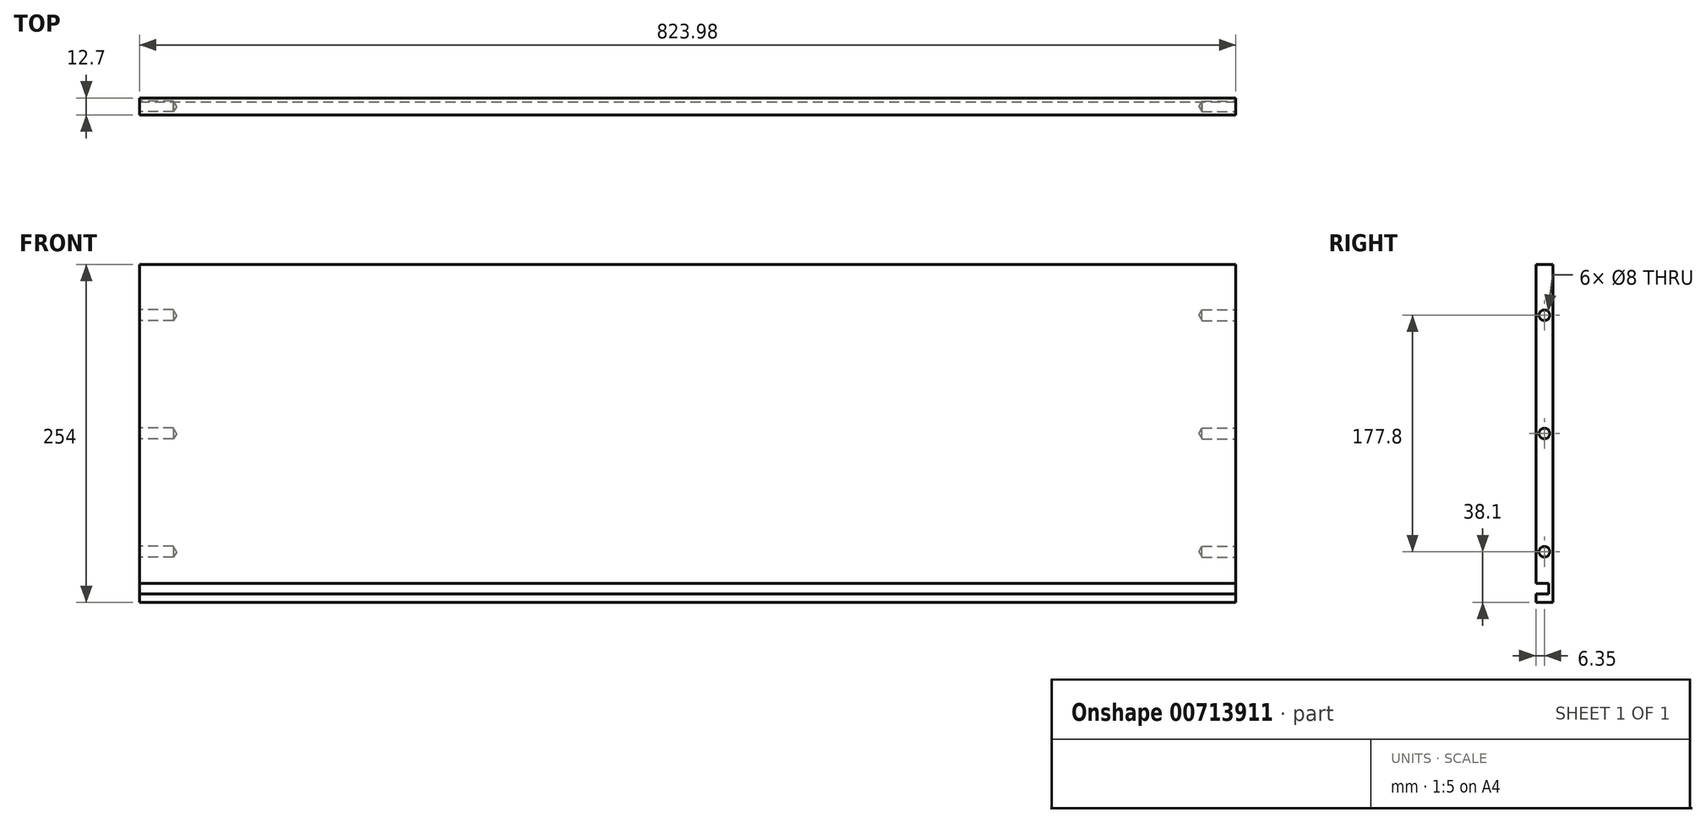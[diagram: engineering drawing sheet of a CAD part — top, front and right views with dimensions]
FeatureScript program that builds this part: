
annotation { "Feature Type Name" : "Feature", "Feature Type Description" : "" }
export const myFeature = defineFeature(function(context is Context, id is Id, definition is map)
    precondition{}
    {
        {
            var Q0;
            Q0=qCreatedBy(makeId("Front.planeOp"),FACE);
            var sketch = newSketch(context, id + "F0", { "sketchPlane" : qUnion([Q0])});
            skLineSegment(sketch, "E0.bottom", {"start": v(411.99, 127) * mm, "end": v(-411.99, 127) * mm});
            skLineSegment(sketch, "E0.top", {"start": v(411.99, -127) * mm, "end": v(-411.99, -127) * mm});
            skLineSegment(sketch, "E0.left", {"start": v(411.99, 127) * mm, "end": v(411.99, -127) * mm});
            skLineSegment(sketch, "E0.right", {"start": v(-411.99, 127) * mm, "end": v(-411.99, -127) * mm});
            skPoint(sketch, "E0.middle", {"position": v(0, 0) * mm});
            skSolve(sketch);
        }
        {
            var Q0;
            Q0=makeQuery(id+"F0.imprint","IMPRINT",FACE,{"disambiguationData":[TD([[makeQuery(id+"F0.imprint","IMPRINT",EDGE,{"derivedFrom":sQuery(id+"F0.wireOp",EDGE,"E0.bottom")}),1.0]])]});
            extrude(context, id + "F1", {"entities" : qUnion([Q0]), "depth" : 12.7 * mm, "offsetDistance" : 25.4 * mm});
        }
        {
            var Q0;
            Q0=makeQuery(id+"F1.opExtrude","CAP_FACE",FACE,{"disambiguationData":[OSD([sQuery(id+"F0.wireOp",EDGE,"E0.bottom"),sQuery(id+"F0.wireOp",EDGE,"E0.top"),sQuery(id+"F0.wireOp",EDGE,"E0.left"),sQuery(id+"F0.wireOp",EDGE,"E0.right")])],"isStart":false});
            var sketch = newSketch(context, id + "F2", { "sketchPlane" : qUnion([Q0])});
            skLineSegment(sketch, "E1", {"start": v(-411.99, -127) * mm, "end": v(-411.99, -120.65) * mm});
            skLineSegment(sketch, "E2.bottom", {"start": v(-411.99, -120.65) * mm, "end": v(411.99, -120.65) * mm});
            skLineSegment(sketch, "E2.top", {"start": v(-411.99, -112.78) * mm, "end": v(411.99, -112.78) * mm});
            skLineSegment(sketch, "E2.left", {"start": v(-411.99, -120.65) * mm, "end": v(-411.99, -112.78) * mm});
            skLineSegment(sketch, "E2.right", {"start": v(411.99, -120.65) * mm, "end": v(411.99, -112.78) * mm});
            skSolve(sketch);
        }
        {
            var Q0;
            Q0=makeQuery(id+"F2.imprint","IMPRINT",FACE,{"disambiguationData":[TD([[makeQuery(id+"F2.imprint","IMPRINT",EDGE,{"derivedFrom":sQuery(id+"F2.wireOp",EDGE,"E2.bottom")}),1.0]])]});
            extrude(context, id + "F3", {"entities" : qUnion([Q0]), "operationType" : NewBodyOperationType.REMOVE, "oppositeDirection" : true, "depth" : 9.65 * mm, "offsetDistance" : 25.4 * mm});
        }
        {
            var Q0;
            Q0=makeQuery(id+"F1.opExtrude","SWEPT_FACE",FACE,{"disambiguationData":[OSD([sQuery(id+"F0.wireOp",EDGE,"E0.right")])]});
            var sketch = newSketch(context, id + "F4", { "sketchPlane" : qUnion([Q0])});
            skLineSegment(sketch, "E3", {"start": v(6.35, 127) * mm, "end": v(6.35, 88.9) * mm});
            skLineSegment(sketch, "E4", {"start": v(6.35, 88.9) * mm, "end": v(6.35, 0) * mm});
            skLineSegment(sketch, "E5", {"start": v(6.35, 0) * mm, "end": v(6.35, -88.9) * mm});
            skPoint(sketch, "E6", {"position": v(6.35, 88.9) * mm});
            skPoint(sketch, "E7", {"position": v(6.35, 0) * mm});
            skPoint(sketch, "E8", {"position": v(6.35, -88.9) * mm});
            skSolve(sketch);
        }
        {
            var Q0;
            Q0=sQuery(id+"F4.wireOp",VERTEX,"E6");
            var Q1;
            Q1=sQuery(id+"F4.wireOp",VERTEX,"E7");
            var Q2;
            Q2=sQuery(id+"F4.wireOp",VERTEX,"E8");
            var Q3;
            Q3=makeQuery(id+"F1.opExtrude","SWEPT_BODY",BODY,{"disambiguationData":[OSD([sQuery(id+"F0.wireOp",EDGE,"E0.bottom"),sQuery(id+"F0.wireOp",EDGE,"E0.top"),sQuery(id+"F0.wireOp",EDGE,"E0.left"),sQuery(id+"F0.wireOp",EDGE,"E0.right")])]});
            hole(context, id + "F5", {"style" : HoleStyle.SIMPLE, "endStyle" : HoleEndStyle.BLIND, "holeDiameter" : 8 * mm, "majorDiameter" : 6.35 * mm, "holeDepth" : 25.4 * mm, "isTappedThrough" : true, "tappedDepth" : 12.7 * mm, "tapClearance" : 3, "startFromSketch" : true, "locations" : qUnion([Q0, Q1, Q2]), "scope" : qUnion([Q3])});
        }
        {
            var Q0;
            Q0=makeQuery(id+"F1.opExtrude","SWEPT_FACE",FACE,{"disambiguationData":[OSD([sQuery(id+"F0.wireOp",EDGE,"E0.left")])]});
            var sketch = newSketch(context, id + "F6", { "sketchPlane" : qUnion([Q0])});
            skLineSegment(sketch, "E9", {"start": v(-6.35, 127) * mm, "end": v(-6.35, 88.9) * mm});
            skLineSegment(sketch, "E10", {"start": v(-6.35, 88.9) * mm, "end": v(-6.35, 0) * mm});
            skLineSegment(sketch, "E11", {"start": v(-6.35, 0) * mm, "end": v(-6.35, -88.9) * mm});
            skPoint(sketch, "E12", {"position": v(-6.35, 88.9) * mm});
            skPoint(sketch, "E13", {"position": v(-6.35, 0) * mm});
            skPoint(sketch, "E14", {"position": v(-6.35, -88.9) * mm});
            skSolve(sketch);
        }
        {
            var Q0;
            Q0=sQuery(id+"F6.wireOp",VERTEX,"E12");
            var Q1;
            Q1=sQuery(id+"F6.wireOp",VERTEX,"E13");
            var Q2;
            Q2=sQuery(id+"F6.wireOp",VERTEX,"E14");
            var Q3;
            Q3=makeQuery(id+"F1.opExtrude","SWEPT_BODY",BODY,{"disambiguationData":[OSD([sQuery(id+"F0.wireOp",EDGE,"E0.bottom"),sQuery(id+"F0.wireOp",EDGE,"E0.top"),sQuery(id+"F0.wireOp",EDGE,"E0.left"),sQuery(id+"F0.wireOp",EDGE,"E0.right")])]});
            hole(context, id + "F7", {"style" : HoleStyle.SIMPLE, "endStyle" : HoleEndStyle.BLIND, "holeDiameter" : 8 * mm, "majorDiameter" : 6.35 * mm, "holeDepth" : 25.4 * mm, "isTappedThrough" : true, "tappedDepth" : 12.7 * mm, "tapClearance" : 3, "startFromSketch" : true, "locations" : qUnion([Q0, Q1, Q2]), "scope" : qUnion([Q3])});
        }
    });
